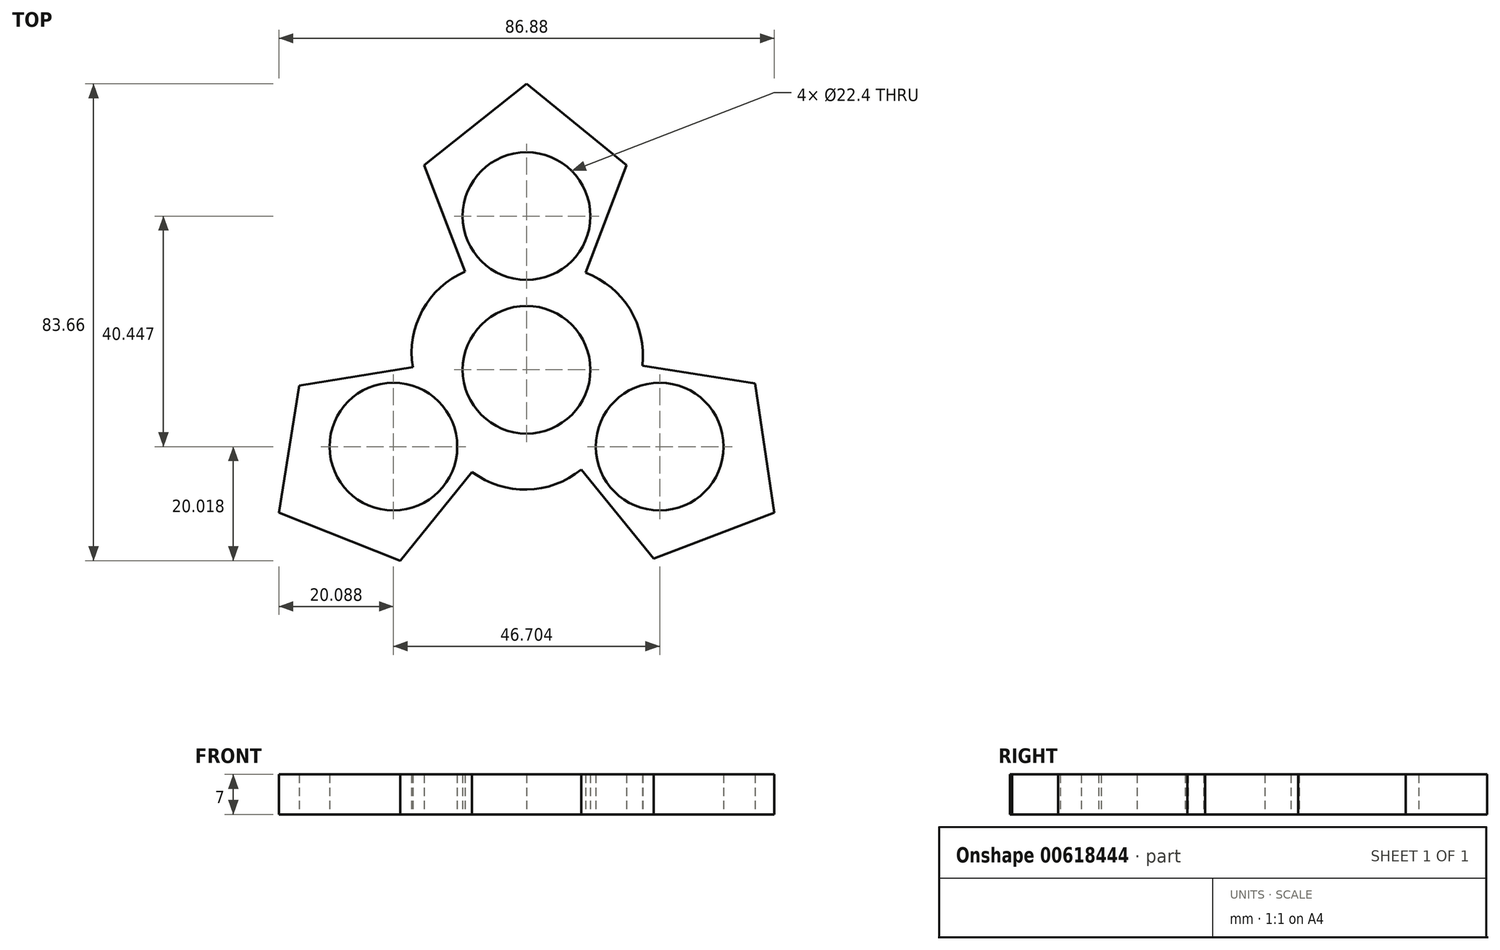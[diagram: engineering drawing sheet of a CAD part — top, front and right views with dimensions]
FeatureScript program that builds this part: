
annotation { "Feature Type Name" : "Feature", "Feature Type Description" : "" }
export const myFeature = defineFeature(function(context is Context, id is Id, definition is map)
    precondition{}
    {
        {
            var Q0;
            Q0=qCreatedBy(makeId("Top.planeOp"),FACE);
            var sketch = newSketch(context, id + "F0", { "sketchPlane" : qUnion([Q0])});
            skCircle(sketch, "E0", {"center": v(0, 0) * mm, "radius": 11.2 * mm});
            skArc(sketch, "E1", {"start": v(-6.6, -11.43) * mm, "mid": v(11.8, 5.93) * mm, "end": v(-13.11, 1.53) * mm});
            skCircle(sketch, "E2", {"center": v(0, 26.96) * mm, "radius": 11.2 * mm});
            skCircle(sketch, "E3", {"center": v(0, 26.96) * mm, "radius": 13.2 * mm});
            skCircle(sketch, "E4.1.2", {"center": v(-23.35, -13.48) * mm, "radius": 13.2 * mm});
            skCircle(sketch, "E4.1.3", {"center": v(-23.35, -13.48) * mm, "radius": 11.2 * mm});
            skCircle(sketch, "E4.2.2", {"center": v(23.35, -13.48) * mm, "radius": 13.2 * mm});
            skCircle(sketch, "E4.2.3", {"center": v(23.35, -13.48) * mm, "radius": 11.2 * mm});
            skLineSegment(sketch, "E5", {"start": v(-8.12, 10.4) * mm, "end": v(-17.95, 35.9) * mm});
            skLineSegment(sketch, "E6", {"start": v(-17.95, 35.9) * mm, "end": v(0, 50.16) * mm});
            skLineSegment(sketch, "E7", {"start": v(0, 50.16) * mm, "end": v(17.54, 35.9) * mm});
            skLineSegment(sketch, "E8", {"start": v(17.54, 35.9) * mm, "end": v(7.88, 10.6) * mm});
            skLineSegment(sketch, "E9.1.0", {"start": v(-43.44, -25.08) * mm, "end": v(-39.87, -2.76) * mm});
            skLineSegment(sketch, "E9.1.1", {"start": v(-22.12, -33.5) * mm, "end": v(-43.44, -25.08) * mm});
            skLineSegment(sketch, "E9.1.2", {"start": v(-4.95, -12.24) * mm, "end": v(-22.12, -33.5) * mm});
            skLineSegment(sketch, "E9.1.3", {"start": v(-39.87, -2.76) * mm, "end": v(-13.11, 1.53) * mm});
            skLineSegment(sketch, "E9.2.0", {"start": v(43.44, -25.08) * mm, "end": v(22.33, -33.15) * mm});
            skLineSegment(sketch, "E9.2.1", {"start": v(40.07, -2.4) * mm, "end": v(43.44, -25.08) * mm});
            skLineSegment(sketch, "E9.2.2", {"start": v(13.07, 1.83) * mm, "end": v(40.07, -2.4) * mm});
            skLineSegment(sketch, "E9.2.3", {"start": v(22.33, -33.15) * mm, "end": v(5.23, -12.12) * mm});
            skArc(sketch, "E10", {"start": v(-9.55, -17.93) * mm, "mid": v(0.1, -21.02) * mm, "end": v(9.6, -17.49) * mm});
            skArc(sketch, "E11.1.0", {"start": v(20.3, 0.7) * mm, "mid": v(18.15, 10.6) * mm, "end": v(10.35, 17.05) * mm});
            skArc(sketch, "E11.2.0", {"start": v(-10.75, 17.24) * mm, "mid": v(-18.25, 10.42) * mm, "end": v(-19.94, 0.43) * mm});
            skSolve(sketch);
        }
        {
            var Q0;
            Q0=qCreatedBy(makeId("Top.planeOp"),FACE);
            var sketch = newSketch(context, id + "F1", { "sketchPlane" : qUnion([Q0])});
            skSolve(sketch);
        }
        {
            var Q0;
            Q0 = qSketchRegion(id + "F1", true);
            var Q1;
            {var subQ11=sQuery(id+"F0.wireOp",EDGE,"E4.1.2");Q1=makeQuery(id+"F0.imprint","IMPRINT",FACE,{"disambiguationData":[TD([[makeQuery(id+"F0.imprint","IMPRINT",EDGE,{"derivedFrom":subQ11}),-1.0]])]});}
            var Q2;
            {var subQ4=sQuery(id+"F0.wireOp",EDGE,"E3");Q2=makeQuery(id+"F0.imprint","IMPRINT",FACE,{"disambiguationData":[TD([[makeQuery(id+"F0.imprint","IMPRINT",EDGE,{"derivedFrom":subQ4}),-1.0]])]});}
            var Q3;
            {var subQ5=sQuery(id+"F0.wireOp",EDGE,"E11.1.0");Q3=makeQuery(id+"F0.imprint","IMPRINT",FACE,{"disambiguationData":[TD([[makeQuery(id+"F0.imprint","IMPRINT",EDGE,{"derivedFrom":subQ5}),1.0]])]});}
            var Q4;
            Q4=makeQuery(id+"F0.imprint","IMPRINT",FACE,{"disambiguationData":[TD([[makeQuery(id+"F0.imprint","IMPRINT",EDGE,{"derivedFrom":sQuery(id+"F0.wireOp",EDGE,"E4.2.2")}),1.0]])]});
            var Q5;
            {var subQ1=sQuery(id+"F0.wireOp",EDGE,"E4.2.2");Q5=makeQuery(id+"F0.imprint","IMPRINT",FACE,{"disambiguationData":[TD([[makeQuery(id+"F0.imprint","IMPRINT",EDGE,{"derivedFrom":subQ1}),-1.0]])]});}
            var Q6;
            {var subQ5=sQuery(id+"F0.wireOp",EDGE,"E10");Q6=makeQuery(id+"F0.imprint","IMPRINT",FACE,{"disambiguationData":[TD([[makeQuery(id+"F0.imprint","IMPRINT",EDGE,{"derivedFrom":subQ5}),1.0]])]});}
            var Q7;
            Q7=makeQuery(id+"F0.imprint","IMPRINT",FACE,{"disambiguationData":[TD([[makeQuery(id+"F0.imprint","IMPRINT",EDGE,{"derivedFrom":sQuery(id+"F0.wireOp",EDGE,"E4.1.2")}),1.0]])]});
            var Q8;
            {var subQ5=sQuery(id+"F0.wireOp",EDGE,"E11.2.0");Q8=makeQuery(id+"F0.imprint","IMPRINT",FACE,{"disambiguationData":[TD([[makeQuery(id+"F0.imprint","IMPRINT",EDGE,{"derivedFrom":subQ5}),1.0]])]});}
            var Q9;
            Q9=makeQuery(id+"F0.imprint","IMPRINT",FACE,{"disambiguationData":[TD([[makeQuery(id+"F0.imprint","IMPRINT",EDGE,{"derivedFrom":sQuery(id+"F0.wireOp",EDGE,"E2")}),-1.0]])]});
            extrude(context, id + "F2", {"entities" : qUnion([Q0, Q1, Q2, Q3, Q4, Q5, Q6, Q7, Q8, Q9]), "depth" : 7 * mm, "offsetDistance" : 25 * mm});
        }
    });
